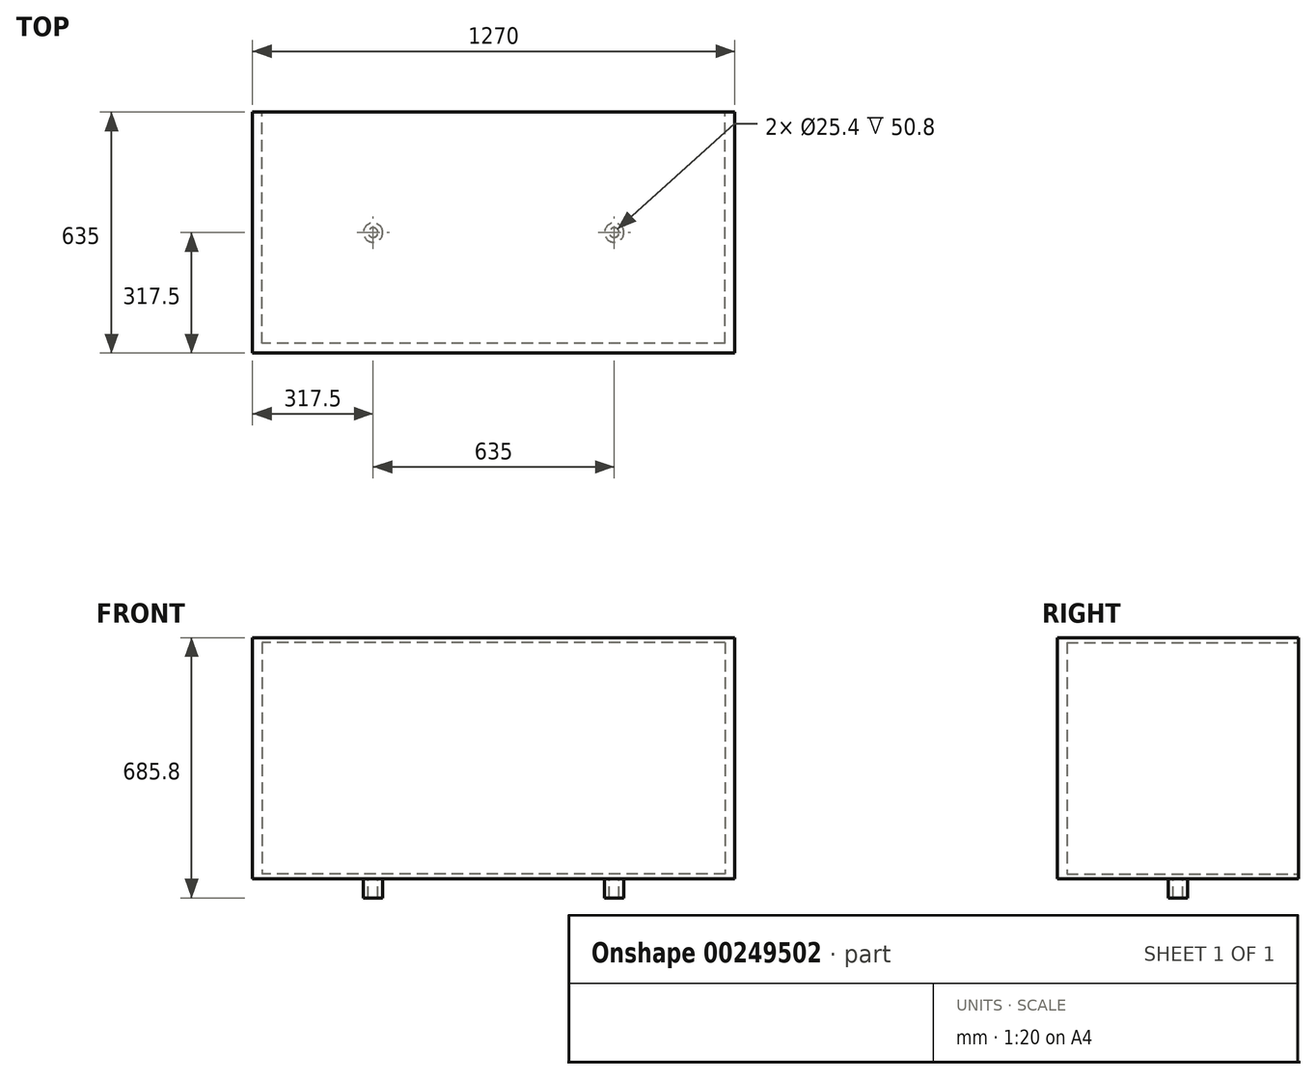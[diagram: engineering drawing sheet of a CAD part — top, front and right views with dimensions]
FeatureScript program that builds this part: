
annotation { "Feature Type Name" : "Feature", "Feature Type Description" : "" }
export const myFeature = defineFeature(function(context is Context, id is Id, definition is map)
    precondition{}
    {
        {
            var Q0;
            Q0=qCreatedBy(makeId("Front.planeOp"),FACE);
            var sketch = newSketch(context, id + "F0", { "sketchPlane" : qUnion([Q0])});
            skLineSegment(sketch, "E0.bottom", {"start": v(635, 317.5) * mm, "end": v(-635, 317.5) * mm});
            skLineSegment(sketch, "E0.top", {"start": v(635, -317.5) * mm, "end": v(-635, -317.5) * mm});
            skLineSegment(sketch, "E0.left", {"start": v(635, 317.5) * mm, "end": v(635, -317.5) * mm});
            skLineSegment(sketch, "E0.right", {"start": v(-635, 317.5) * mm, "end": v(-635, -317.5) * mm});
            skPoint(sketch, "E0.middle", {"position": v(0, 0) * mm});
            skLineSegment(sketch, "E1.bottom", {"start": v(609.6, 304.8) * mm, "end": v(-609.6, 304.8) * mm});
            skLineSegment(sketch, "E1.top", {"start": v(609.6, -304.8) * mm, "end": v(-609.6, -304.8) * mm});
            skLineSegment(sketch, "E1.left", {"start": v(609.6, 304.8) * mm, "end": v(609.6, -304.8) * mm});
            skLineSegment(sketch, "E1.right", {"start": v(-609.6, 304.8) * mm, "end": v(-609.6, -304.8) * mm});
            skSolve(sketch);
        }
        {
            var Q0;
            Q0=makeQuery(id+"F0.imprint","IMPRINT",FACE,{"disambiguationData":[TD([[makeQuery(id+"F0.imprint","IMPRINT",EDGE,{"derivedFrom":sQuery(id+"F0.wireOp",EDGE,"E0.bottom")}),1.0]])]});
            var Q1;
            Q1=makeQuery(id+"F0.imprint","IMPRINT",FACE,{"disambiguationData":[TD([[makeQuery(id+"F0.imprint","IMPRINT",EDGE,{"derivedFrom":sQuery(id+"F0.wireOp",EDGE,"E1.bottom")}),1.0]])]});
            extrude(context, id + "F1", {"entities" : qUnion([Q0, Q1]), "depth" : 635 * mm});
        }
        {
            var Q0;
            Q0=makeQuery(id+"F0.imprint","IMPRINT",FACE,{"disambiguationData":[TD([[makeQuery(id+"F0.imprint","IMPRINT",EDGE,{"derivedFrom":sQuery(id+"F0.wireOp",EDGE,"E1.bottom")}),1.0]])]});
            extrude(context, id + "F2", {"entities" : qUnion([Q0]), "operationType" : NewBodyOperationType.REMOVE, "depth" : 609.6 * mm});
        }
        {
            var Q0;
            Q0=makeQuery(id+"F1.opExtrude","SWEPT_FACE",FACE,{"disambiguationData":[OSD([sQuery(id+"F0.wireOp",EDGE,"E0.top")])]});
            var sketch = newSketch(context, id + "F3", { "sketchPlane" : qUnion([Q0])});
            skLineSegment(sketch, "E2", {"start": v(0, 0) * mm, "end": v(0, 635) * mm, "construction": true});
            skLineSegment(sketch, "E3.bottom", {"start": v(635, 635) * mm, "end": v(317.5, 635) * mm, "construction": true});
            skLineSegment(sketch, "E3.top", {"start": v(635, 317.5) * mm, "end": v(317.5, 317.5) * mm, "construction": true});
            skLineSegment(sketch, "E3.left", {"start": v(635, 635) * mm, "end": v(635, 317.5) * mm, "construction": true});
            skLineSegment(sketch, "E3.right", {"start": v(317.5, 635) * mm, "end": v(317.5, 317.5) * mm, "construction": true});
            skLineSegment(sketch, "E4.bottom", {"start": v(-635, 635) * mm, "end": v(-317.5, 635) * mm, "construction": true});
            skLineSegment(sketch, "E4.top", {"start": v(-635, 317.5) * mm, "end": v(-317.5, 317.5) * mm, "construction": true});
            skLineSegment(sketch, "E4.left", {"start": v(-635, 635) * mm, "end": v(-635, 317.5) * mm, "construction": true});
            skLineSegment(sketch, "E4.right", {"start": v(-317.5, 635) * mm, "end": v(-317.5, 317.5) * mm, "construction": true});
            skCircle(sketch, "E5", {"center": v(317.5, 317.5) * mm, "radius": 25.4 * mm});
            skCircle(sketch, "E6", {"center": v(317.5, 317.5) * mm, "radius": 12.7 * mm});
            skCircle(sketch, "E7", {"center": v(-317.5, 317.5) * mm, "radius": 12.7 * mm});
            skCircle(sketch, "E8", {"center": v(-317.5, 317.5) * mm, "radius": 25.4 * mm});
            skSolve(sketch);
        }
        {
            var Q0;
            Q0=makeQuery(id+"F3.imprint","IMPRINT",FACE,{"disambiguationData":[TD([[makeQuery(id+"F3.imprint","IMPRINT",EDGE,{"derivedFrom":sQuery(id+"F3.wireOp",EDGE,"E5")}),1.0]])]});
            var Q1;
            Q1=makeQuery(id+"F3.imprint","IMPRINT",FACE,{"disambiguationData":[TD([[makeQuery(id+"F3.imprint","IMPRINT",EDGE,{"derivedFrom":sQuery(id+"F3.wireOp",EDGE,"E7")}),-1.0]])]});
            extrude(context, id + "F4", {"entities" : qUnion([Q0, Q1]), "operationType" : NewBodyOperationType.ADD, "depth" : 50.8 * mm});
        }
    });
